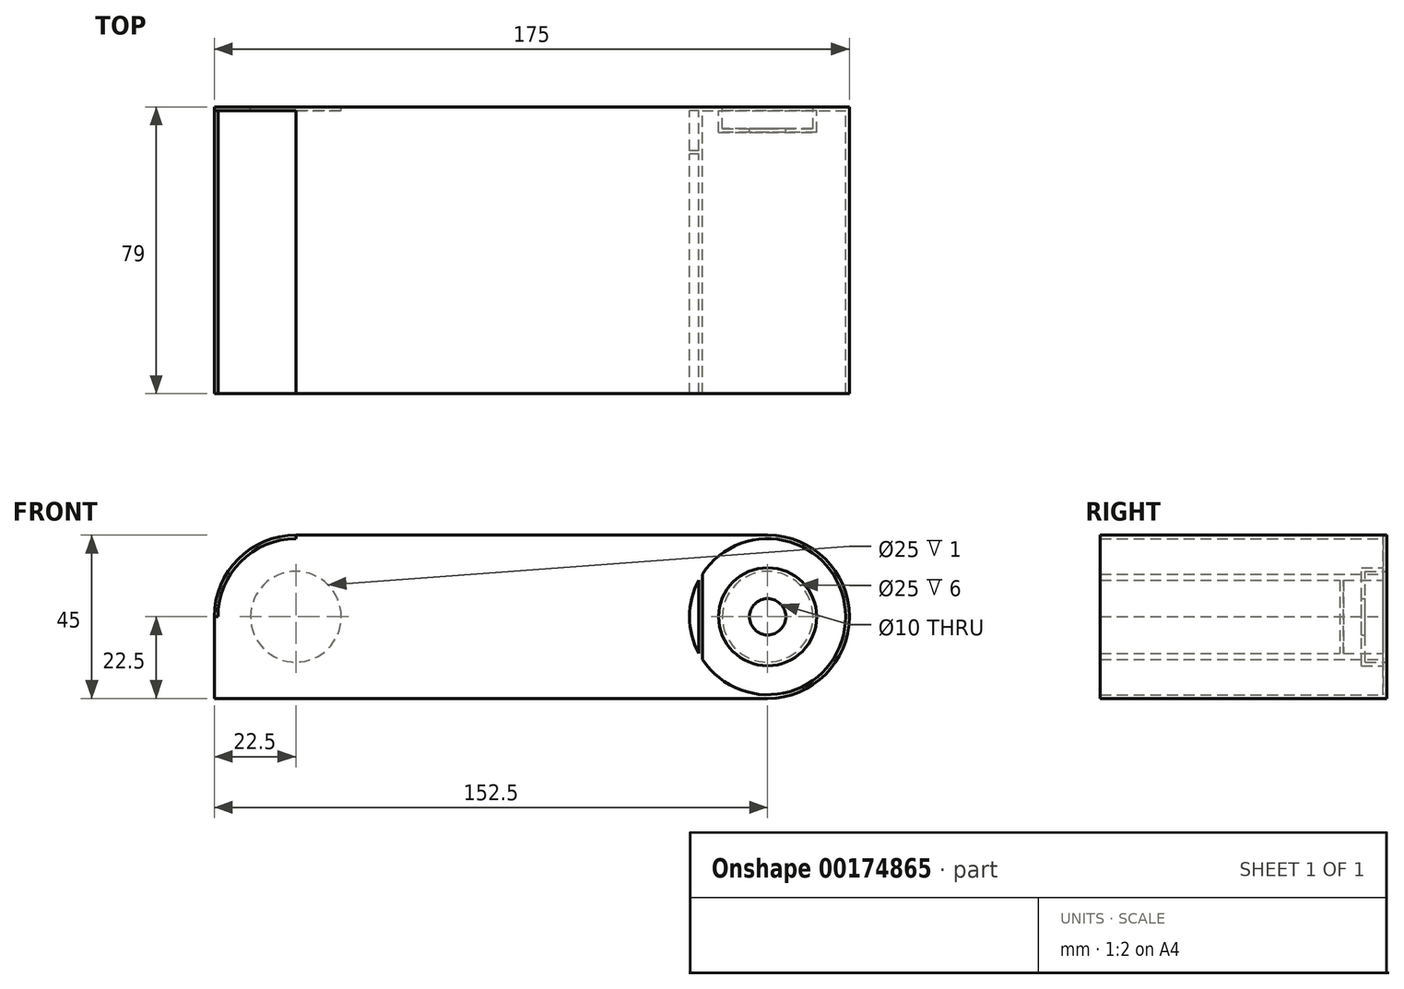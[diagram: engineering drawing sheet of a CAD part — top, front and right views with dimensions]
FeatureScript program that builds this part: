
annotation { "Feature Type Name" : "Feature", "Feature Type Description" : "" }
export const myFeature = defineFeature(function(context is Context, id is Id, definition is map)
    precondition{}
    {
        {
            var Q0;
            Q0=qCreatedBy(makeId("Front.planeOp"),FACE);
            var sketch = newSketch(context, id + "F0", { "sketchPlane" : qUnion([Q0])});
            skLineSegment(sketch, "E0.bottom", {"start": v(82.5, 22.5) * mm, "end": v(-82.5, 22.5) * mm});
            skLineSegment(sketch, "E0.top", {"start": v(82.5, -22.5) * mm, "end": v(-82.5, -22.5) * mm});
            skLineSegment(sketch, "E0.left", {"start": v(82.5, 22.5) * mm, "end": v(82.5, -22.5) * mm});
            skLineSegment(sketch, "E0.right", {"start": v(-82.5, 22.5) * mm, "end": v(-82.5, -22.5) * mm});
            skPoint(sketch, "E0.middle", {"position": v(0, 0) * mm});
            skCircle(sketch, "E1", {"center": v(-65, 0) * mm, "radius": 12.5 * mm});
            skCircle(sketch, "E2", {"center": v(65, 0) * mm, "radius": 12.5 * mm});
            skSolve(sketch);
        }
        {
            var Q0;
            Q0=qSketchRegion(id+"F0",true);
            extrude(context, id + "F1", {"entities" : qUnion([Q0]), "depth" : 1 * mm});
        }
        {
            var Q0;
            Q0=makeQuery(id+"F1.opExtrude","CAP_FACE",FACE,{"disambiguationData":[OSD([sQuery(id+"F0.wireOp",EDGE,"E0.bottom"),sQuery(id+"F0.wireOp",EDGE,"E0.top"),sQuery(id+"F0.wireOp",EDGE,"E0.left"),sQuery(id+"F0.wireOp",EDGE,"E0.right"),sQuery(id+"F0.wireOp",EDGE,"E1"),sQuery(id+"F0.wireOp",EDGE,"E2")])],"isStart":false});
            var sketch = newSketch(context, id + "F2", { "sketchPlane" : qUnion([Q0])});
            skArc(sketch, "E3", {"start": v(65, -22.5) * mm, "mid": v(87.5, 0) * mm, "end": v(65, 22.5) * mm});
            skPoint(sketch, "E4.end.orphan", {"position": v(-82.5, 0) * mm});
            skArc(sketch, "E5", {"start": v(-65, 22.5) * mm, "mid": v(-87.5, 0) * mm, "end": v(-65, -22.5) * mm});
            skLineSegment(sketch, "E6", {"start": v(-65, 22.5) * mm, "end": v(-65, 14.96) * mm});
            skLineSegment(sketch, "E7", {"start": v(-65, 14.96) * mm, "end": v(-75.45, 11.76) * mm});
            skLineSegment(sketch, "E8", {"start": v(-75.45, 11.76) * mm, "end": v(-79.56, 6.47) * mm});
            skLineSegment(sketch, "E9", {"start": v(-79.56, 6.47) * mm, "end": v(-79.56, 0) * mm});
            skLineSegment(sketch, "E10", {"start": v(-79.56, 0) * mm, "end": v(-76.59, -7.8) * mm});
            skLineSegment(sketch, "E11", {"start": v(-76.59, -7.8) * mm, "end": v(-72.84, -12.91) * mm});
            skLineSegment(sketch, "E12", {"start": v(-72.84, -12.91) * mm, "end": v(-67.48, -15.7) * mm});
            skLineSegment(sketch, "E13", {"start": v(-67.48, -15.7) * mm, "end": v(-65, -22.5) * mm});
            skLineSegment(sketch, "E14", {"start": v(65, 22.5) * mm, "end": v(71.47, 16.28) * mm});
            skLineSegment(sketch, "E15", {"start": v(71.47, 16.28) * mm, "end": v(77.4, 9.11) * mm});
            skLineSegment(sketch, "E16", {"start": v(77.4, 9.11) * mm, "end": v(80.4, 2.14) * mm});
            skLineSegment(sketch, "E17", {"start": v(80.4, 2.14) * mm, "end": v(80.4, -5.23) * mm});
            skLineSegment(sketch, "E18", {"start": v(80.4, -5.23) * mm, "end": v(78.4, -12.15) * mm});
            skLineSegment(sketch, "E19", {"start": v(78.4, -12.15) * mm, "end": v(74.66, -14.4) * mm});
            skLineSegment(sketch, "E20", {"start": v(74.66, -14.4) * mm, "end": v(68.4, -19.1) * mm});
            skLineSegment(sketch, "E21", {"start": v(68.4, -19.1) * mm, "end": v(65, -22.5) * mm});
            skSolve(sketch);
        }
        {
            var Q0;
            Q0=qSketchRegion(id+"F2",true);
            extrude(context, id + "F3", {"entities" : qUnion([Q0]), "operationType" : NewBodyOperationType.ADD, "oppositeDirection" : true, "depth" : 1 * mm});
        }
        {
            var Q0;
            {var subQ1=makeQuery(id+"F1.opExtrude","CAP_EDGE",EDGE,{"disambiguationData":[OSD([sQuery(id+"F0.wireOp",EDGE,"E0.bottom")])],"isStart":false});var subQ3=makeQuery(id+"F1.opExtrude","CAP_EDGE",EDGE,{"disambiguationData":[OSD([sQuery(id+"F0.wireOp",EDGE,"E0.right")])],"isStart":false});var subQ5=makeQuery(id+"F2.imprint","INTERSECT",VERTEX,{"derivedFrom":[subQ1,subQ3]});Q0=makeQuery(id+"F2.imprint","IMPRINT",FACE,{"disambiguationData":[TD([[makeQuery(id+"F2.imprint","IMPRINT",EDGE,{"disambiguationData":[TD([[subQ5,-1.0]])],"derivedFrom":subQ3}),1.0]])]});}
            extrude(context, id + "F4", {"entities" : qUnion([Q0]), "operationType" : NewBodyOperationType.REMOVE, "oppositeDirection" : true, "depth" : 25 * mm});
        }
        {
            var Q0;
            {var subQ1=makeQuery(id+"F1.opExtrude","CAP_EDGE",EDGE,{"disambiguationData":[OSD([sQuery(id+"F0.wireOp",EDGE,"E0.top")])],"isStart":false});var subQ3=makeQuery(id+"F1.opExtrude","CAP_EDGE",EDGE,{"disambiguationData":[OSD([sQuery(id+"F0.wireOp",EDGE,"E0.left")])],"isStart":false});var subQ5=makeQuery(id+"F2.imprint","INTERSECT",VERTEX,{"derivedFrom":[subQ1,subQ3]});Q0=makeQuery(id+"F2.imprint","IMPRINT",FACE,{"disambiguationData":[TD([[makeQuery(id+"F2.imprint","IMPRINT",EDGE,{"disambiguationData":[TD([[subQ5,1.0]])],"derivedFrom":subQ3}),-1.0]])]});}
            var Q1;
            {var subQ1=makeQuery(id+"F1.opExtrude","CAP_EDGE",EDGE,{"disambiguationData":[OSD([sQuery(id+"F0.wireOp",EDGE,"E0.bottom")])],"isStart":false});var subQ3=makeQuery(id+"F1.opExtrude","CAP_EDGE",EDGE,{"disambiguationData":[OSD([sQuery(id+"F0.wireOp",EDGE,"E0.left")])],"isStart":false});var subQ5=makeQuery(id+"F2.imprint","INTERSECT",VERTEX,{"derivedFrom":[subQ1,subQ3]});Q1=makeQuery(id+"F2.imprint","IMPRINT",FACE,{"disambiguationData":[TD([[makeQuery(id+"F2.imprint","IMPRINT",EDGE,{"disambiguationData":[TD([[subQ5,-1.0]])],"derivedFrom":subQ3}),-1.0]])]});}
            var Q2;
            {var subQ1=makeQuery(id+"F1.opExtrude","CAP_EDGE",EDGE,{"disambiguationData":[OSD([sQuery(id+"F0.wireOp",EDGE,"E0.top")])],"isStart":false});var subQ3=makeQuery(id+"F1.opExtrude","CAP_EDGE",EDGE,{"disambiguationData":[OSD([sQuery(id+"F0.wireOp",EDGE,"E0.right")])],"isStart":false});var subQ5=makeQuery(id+"F2.imprint","INTERSECT",VERTEX,{"derivedFrom":[subQ1,subQ3]});Q2=makeQuery(id+"F2.imprint","IMPRINT",FACE,{"disambiguationData":[TD([[makeQuery(id+"F2.imprint","IMPRINT",EDGE,{"disambiguationData":[TD([[subQ5,1.0]])],"derivedFrom":subQ3}),1.0]])]});}
            extrude(context, id + "F5", {"entities" : qUnion([Q0, Q1, Q2]), "operationType" : NewBodyOperationType.REMOVE, "oppositeDirection" : true, "depth" : 25 * mm});
        }
        {
            var Q0;
            Q0=makeQuery(id+"F3.boolean.opBoolean","MERGE",FACE,{"derivedFrom":[makeQuery(id+"F1.opExtrude","CAP_FACE",FACE,{"disambiguationData":[OSD([sQuery(id+"F0.wireOp",EDGE,"E0.bottom"),sQuery(id+"F0.wireOp",EDGE,"E0.top"),sQuery(id+"F0.wireOp",EDGE,"E0.left"),sQuery(id+"F0.wireOp",EDGE,"E0.right"),sQuery(id+"F0.wireOp",EDGE,"E1"),sQuery(id+"F0.wireOp",EDGE,"E2")])],"isStart":false}),makeQuery(id+"F3.opExtrude","CAP_FACE",FACE,{"disambiguationData":[OSD([sQuery(id+"F2.wireOp",EDGE,"E3"),sQuery(id+"F2.wireOp",EDGE,"E14"),sQuery(id+"F2.wireOp",EDGE,"E15"),sQuery(id+"F2.wireOp",EDGE,"E16"),sQuery(id+"F2.wireOp",EDGE,"E17"),sQuery(id+"F2.wireOp",EDGE,"E18"),sQuery(id+"F2.wireOp",EDGE,"E19"),sQuery(id+"F2.wireOp",EDGE,"E20"),sQuery(id+"F2.wireOp",EDGE,"E21")])],"isStart":true}),makeQuery(id+"F3.opExtrude","CAP_FACE",FACE,{"disambiguationData":[OSD([sQuery(id+"F2.wireOp",EDGE,"E5"),sQuery(id+"F2.wireOp",EDGE,"E6"),sQuery(id+"F2.wireOp",EDGE,"E7"),sQuery(id+"F2.wireOp",EDGE,"E8"),sQuery(id+"F2.wireOp",EDGE,"E9"),sQuery(id+"F2.wireOp",EDGE,"E10"),sQuery(id+"F2.wireOp",EDGE,"E11"),sQuery(id+"F2.wireOp",EDGE,"E12"),sQuery(id+"F2.wireOp",EDGE,"E13")])],"isStart":true})]});
            var sketch = newSketch(context, id + "F6", { "sketchPlane" : qUnion([Q0])});
            skCircle(sketch, "E22", {"center": v(-65, 0) * mm, "radius": 12.5 * mm});
            skCircle(sketch, "E23", {"center": v(-65, 0) * mm, "radius": 13.5 * mm});
            skCircle(sketch, "E24", {"center": v(65, 0) * mm, "radius": 12.5 * mm});
            skCircle(sketch, "E25", {"center": v(65, 0) * mm, "radius": 13.5 * mm});
            skSolve(sketch);
        }
        {
            var Q0;
            Q0=qSketchRegion(id+"F6",true);
            extrude(context, id + "F7", {"entities" : qUnion([Q0]), "operationType" : NewBodyOperationType.ADD, "depth" : 5 * mm});
        }
        {
            var Q0;
            Q0=makeQuery(id+"F7.opExtrude","CAP_FACE",FACE,{"disambiguationData":[OSD([sQuery(id+"F6.wireOp",EDGE,"E22"),sQuery(id+"F6.wireOp",EDGE,"E23")])],"isStart":false});
            var sketch = newSketch(context, id + "F8", { "sketchPlane" : qUnion([Q0])});
            skCircle(sketch, "E26", {"center": v(-65, 0) * mm, "radius": 13.5 * mm});
            skCircle(sketch, "E27", {"center": v(-65, 0) * mm, "radius": 5 * mm});
            skCircle(sketch, "E28", {"center": v(65, 0) * mm, "radius": 13.5 * mm});
            skCircle(sketch, "E29", {"center": v(65, 0) * mm, "radius": 5 * mm});
            skSolve(sketch);
        }
        {
            var Q0;
            Q0=qSketchRegion(id+"F8",true);
            extrude(context, id + "F9", {"entities" : qUnion([Q0]), "operationType" : NewBodyOperationType.ADD, "depth" : 1 * mm});
        }
        {
            var Q0;
            Q0=makeQuery(id+"F3.boolean.opBoolean","MERGE",FACE,{"derivedFrom":[makeQuery(id+"F1.opExtrude","CAP_FACE",FACE,{"disambiguationData":[OSD([sQuery(id+"F0.wireOp",EDGE,"E0.bottom"),sQuery(id+"F0.wireOp",EDGE,"E0.top"),sQuery(id+"F0.wireOp",EDGE,"E0.left"),sQuery(id+"F0.wireOp",EDGE,"E0.right"),sQuery(id+"F0.wireOp",EDGE,"E1"),sQuery(id+"F0.wireOp",EDGE,"E2")])],"isStart":false}),makeQuery(id+"F3.opExtrude","CAP_FACE",FACE,{"disambiguationData":[OSD([sQuery(id+"F2.wireOp",EDGE,"E3"),sQuery(id+"F2.wireOp",EDGE,"E14"),sQuery(id+"F2.wireOp",EDGE,"E15"),sQuery(id+"F2.wireOp",EDGE,"E16"),sQuery(id+"F2.wireOp",EDGE,"E17"),sQuery(id+"F2.wireOp",EDGE,"E18"),sQuery(id+"F2.wireOp",EDGE,"E19"),sQuery(id+"F2.wireOp",EDGE,"E20"),sQuery(id+"F2.wireOp",EDGE,"E21")])],"isStart":true}),makeQuery(id+"F3.opExtrude","CAP_FACE",FACE,{"disambiguationData":[OSD([sQuery(id+"F2.wireOp",EDGE,"E5"),sQuery(id+"F2.wireOp",EDGE,"E6"),sQuery(id+"F2.wireOp",EDGE,"E7"),sQuery(id+"F2.wireOp",EDGE,"E8"),sQuery(id+"F2.wireOp",EDGE,"E9"),sQuery(id+"F2.wireOp",EDGE,"E10"),sQuery(id+"F2.wireOp",EDGE,"E11"),sQuery(id+"F2.wireOp",EDGE,"E12"),sQuery(id+"F2.wireOp",EDGE,"E13")])],"isStart":true})]});
            var sketch = newSketch(context, id + "F10", { "sketchPlane" : qUnion([Q0])});
            skLineSegment(sketch, "E30.bottom", {"start": v(-87.5, 0) * mm, "end": v(-81.94, 0) * mm});
            skLineSegment(sketch, "E30.top", {"start": v(-87.5, -22.5) * mm, "end": v(-65, -22.5) * mm});
            skLineSegment(sketch, "E30.left", {"start": v(-87.5, 0) * mm, "end": v(-87.5, -22.5) * mm});
            skLineSegment(sketch, "E30.right", {"start": v(-65, -18.59) * mm, "end": v(-65, -22.5) * mm});
            skLineSegment(sketch, "E31", {"start": v(-81.94, 0) * mm, "end": v(-80.2, -9.62) * mm});
            skLineSegment(sketch, "E32", {"start": v(-80.2, -9.62) * mm, "end": v(-73.32, -16) * mm});
            skLineSegment(sketch, "E33", {"start": v(-73.32, -16) * mm, "end": v(-65, -18.59) * mm});
            skSolve(sketch);
        }
        {
            var Q0;
            Q0=qSketchRegion(id+"F10",true);
            extrude(context, id + "F11", {"entities" : qUnion([Q0]), "operationType" : NewBodyOperationType.ADD, "oppositeDirection" : true, "depth" : 1 * mm});
        }
        {
            var Q0;
            Q0=makeQuery(id+"F11.boolean.opBoolean","MERGE",FACE,{"derivedFrom":[makeQuery(id+"F3.boolean.opBoolean","MERGE",FACE,{"derivedFrom":[makeQuery(id+"F1.opExtrude","CAP_FACE",FACE,{"disambiguationData":[OSD([sQuery(id+"F0.wireOp",EDGE,"E0.bottom"),sQuery(id+"F0.wireOp",EDGE,"E0.top"),sQuery(id+"F0.wireOp",EDGE,"E0.left"),sQuery(id+"F0.wireOp",EDGE,"E0.right"),sQuery(id+"F0.wireOp",EDGE,"E1"),sQuery(id+"F0.wireOp",EDGE,"E2")])],"isStart":false}),makeQuery(id+"F3.opExtrude","CAP_FACE",FACE,{"disambiguationData":[OSD([sQuery(id+"F2.wireOp",EDGE,"E3"),sQuery(id+"F2.wireOp",EDGE,"E14"),sQuery(id+"F2.wireOp",EDGE,"E15"),sQuery(id+"F2.wireOp",EDGE,"E16"),sQuery(id+"F2.wireOp",EDGE,"E17"),sQuery(id+"F2.wireOp",EDGE,"E18"),sQuery(id+"F2.wireOp",EDGE,"E19"),sQuery(id+"F2.wireOp",EDGE,"E20"),sQuery(id+"F2.wireOp",EDGE,"E21")])],"isStart":true}),makeQuery(id+"F3.opExtrude","CAP_FACE",FACE,{"disambiguationData":[OSD([sQuery(id+"F2.wireOp",EDGE,"E5"),sQuery(id+"F2.wireOp",EDGE,"E6"),sQuery(id+"F2.wireOp",EDGE,"E7"),sQuery(id+"F2.wireOp",EDGE,"E8"),sQuery(id+"F2.wireOp",EDGE,"E9"),sQuery(id+"F2.wireOp",EDGE,"E10"),sQuery(id+"F2.wireOp",EDGE,"E11"),sQuery(id+"F2.wireOp",EDGE,"E12"),sQuery(id+"F2.wireOp",EDGE,"E13")])],"isStart":true})]}),makeQuery(id+"F11.opExtrude","CAP_FACE",FACE,{"disambiguationData":[OSD([sQuery(id+"F10.wireOp",EDGE,"E30.bottom"),sQuery(id+"F10.wireOp",EDGE,"E30.top"),sQuery(id+"F10.wireOp",EDGE,"E30.left"),sQuery(id+"F10.wireOp",EDGE,"E30.right"),sQuery(id+"F10.wireOp",EDGE,"E31"),sQuery(id+"F10.wireOp",EDGE,"E32"),sQuery(id+"F10.wireOp",EDGE,"E33")])],"isStart":true})]});
            var sketch = newSketch(context, id + "F12", { "sketchPlane" : qUnion([Q0])});
            skLineSegment(sketch, "E34.bottom", {"start": v(47, -13.5) * mm, "end": v(-47, -13.5) * mm});
            skLineSegment(sketch, "E34.top", {"start": v(47, -14.5) * mm, "end": v(-47, -14.5) * mm});
            skLineSegment(sketch, "E34.left", {"start": v(47, -13.5) * mm, "end": v(47, -14.5) * mm});
            skLineSegment(sketch, "E34.right", {"start": v(-47, -13.5) * mm, "end": v(-47, -14.5) * mm});
            skPoint(sketch, "E34.middle", {"position": v(0, -14) * mm});
            skLineSegment(sketch, "E35.bottom", {"start": v(-47, -14.5) * mm, "end": v(-46, -14.5) * mm});
            skLineSegment(sketch, "E35.top", {"start": v(-47, 22.5) * mm, "end": v(-46, 22.5) * mm});
            skLineSegment(sketch, "E35.left", {"start": v(-47, -14.5) * mm, "end": v(-47, 22.5) * mm});
            skLineSegment(sketch, "E35.right", {"start": v(-46, -14.5) * mm, "end": v(-46, 22.5) * mm});
            skLineSegment(sketch, "E36.bottom", {"start": v(47, -14.5) * mm, "end": v(46, -14.5) * mm});
            skLineSegment(sketch, "E36.top", {"start": v(47, 22.5) * mm, "end": v(46, 22.5) * mm});
            skLineSegment(sketch, "E36.left", {"start": v(47, -14.5) * mm, "end": v(47, 22.5) * mm});
            skLineSegment(sketch, "E36.right", {"start": v(46, -14.5) * mm, "end": v(46, 22.5) * mm});
            skSolve(sketch);
        }
        {
            var Q0;
            Q0=qSketchRegion(id+"F12",true);
            extrude(context, id + "F13", {"entities" : qUnion([Q0]), "operationType" : NewBodyOperationType.ADD, "depth" : 11 * mm});
        }
        {
            var Q0;
            Q0=makeQuery(id+"F13.opExtrude","CAP_FACE",FACE,{"disambiguationData":[OSD([sQuery(id+"F12.wireOp",EDGE,"E34.bottom"),sQuery(id+"F12.wireOp",EDGE,"E34.top"),sQuery(id+"F12.wireOp",EDGE,"E35.bottom"),sQuery(id+"F12.wireOp",EDGE,"E35.top"),sQuery(id+"F12.wireOp",EDGE,"E35.left"),sQuery(id+"F12.wireOp",EDGE,"E35.right"),sQuery(id+"F12.wireOp",EDGE,"E36.bottom"),sQuery(id+"F12.wireOp",EDGE,"E36.top"),sQuery(id+"F12.wireOp",EDGE,"E36.left"),sQuery(id+"F12.wireOp",EDGE,"E36.right")])],"isStart":false});
            var sketch = newSketch(context, id + "F14", { "sketchPlane" : qUnion([Q0])});
            skLineSegment(sketch, "E37.bottom", {"start": v(-47, -14.5) * mm, "end": v(47, -14.5) * mm});
            skLineSegment(sketch, "E37.top", {"start": v(-47, 22.5) * mm, "end": v(47, 22.5) * mm});
            skLineSegment(sketch, "E37.left", {"start": v(-47, -14.5) * mm, "end": v(-47, 22.5) * mm});
            skLineSegment(sketch, "E37.right", {"start": v(47, -14.5) * mm, "end": v(47, 22.5) * mm});
            skSolve(sketch);
        }
        {
            var Q0;
            Q0=qSketchRegion(id+"F14",true);
            extrude(context, id + "F15", {"entities" : qUnion([Q0]), "operationType" : NewBodyOperationType.ADD, "depth" : 1 * mm});
        }
        {
            var Q0;
            Q0=makeQuery(id+"F15.opExtrude","CAP_FACE",FACE,{"disambiguationData":[OSD([sQuery(id+"F14.wireOp",EDGE,"E37.bottom"),sQuery(id+"F14.wireOp",EDGE,"E37.top"),sQuery(id+"F14.wireOp",EDGE,"E37.left"),sQuery(id+"F14.wireOp",EDGE,"E37.right")])],"isStart":false});
            var sketch = newSketch(context, id + "F16", { "sketchPlane" : qUnion([Q0])});
            skLineSegment(sketch, "E38.bottom", {"start": v(-47, 22.5) * mm, "end": v(-46, 22.5) * mm});
            skLineSegment(sketch, "E38.top", {"start": v(-47, -13.5) * mm, "end": v(-46, -13.5) * mm});
            skLineSegment(sketch, "E38.left", {"start": v(-47, 22.5) * mm, "end": v(-47, -13.5) * mm});
            skLineSegment(sketch, "E38.right", {"start": v(-46, 22.5) * mm, "end": v(-46, -13.5) * mm});
            skLineSegment(sketch, "E39.bottom", {"start": v(47, 22.5) * mm, "end": v(46, 22.5) * mm});
            skLineSegment(sketch, "E39.top", {"start": v(47, -13.5) * mm, "end": v(46, -13.5) * mm});
            skLineSegment(sketch, "E39.left", {"start": v(47, 22.5) * mm, "end": v(47, -13.5) * mm});
            skLineSegment(sketch, "E39.right", {"start": v(46, 22.5) * mm, "end": v(46, -13.5) * mm});
            skSolve(sketch);
        }
        {
            var Q0;
            Q0=qSketchRegion(id+"F16",true);
            extrude(context, id + "F17", {"entities" : qUnion([Q0]), "operationType" : NewBodyOperationType.ADD, "depth" : 66 * mm});
        }
        {
            var Q0;
            {var subQ0=sQuery(id+"F2.wireOp",EDGE,"E14");var subQ1=sQuery(id+"F2.wireOp",EDGE,"E3");var subQ2=sQuery(id+"F0.wireOp",EDGE,"E0.bottom");var subQ3=sQuery(id+"F0.wireOp",EDGE,"E0.left");var subQ5=sQuery(id+"F2.wireOp",EDGE,"E21");var subQ6=sQuery(id+"F0.wireOp",EDGE,"E0.top");var subQ7=sQuery(id+"F2.wireOp",EDGE,"E5");var subQ8=sQuery(id+"F10.wireOp",EDGE,"E30.top");var subQ9=sQuery(id+"F10.wireOp",EDGE,"E30.left");Q0=makeQuery(id+"F13.boolean.opBoolean","SPLIT",FACE,{"disambiguationData":[TD([makeQuery(id+"F1.opExtrude","SWEPT_FACE",FACE,{"disambiguationData":[OSD([subQ6])]})])],"derivedFrom":makeQuery(id+"F11.boolean.opBoolean","MERGE",FACE,{"derivedFrom":[makeQuery(id+"F3.boolean.opBoolean","MERGE",FACE,{"derivedFrom":[makeQuery(id+"F1.opExtrude","CAP_FACE",FACE,{"disambiguationData":[OSD([subQ2,subQ6,subQ3,sQuery(id+"F0.wireOp",EDGE,"E0.right"),sQuery(id+"F0.wireOp",EDGE,"E1"),sQuery(id+"F0.wireOp",EDGE,"E2")])],"isStart":false}),makeQuery(id+"F3.opExtrude","CAP_FACE",FACE,{"disambiguationData":[OSD([subQ1,subQ0,sQuery(id+"F2.wireOp",EDGE,"E15"),sQuery(id+"F2.wireOp",EDGE,"E16"),sQuery(id+"F2.wireOp",EDGE,"E17"),sQuery(id+"F2.wireOp",EDGE,"E18"),sQuery(id+"F2.wireOp",EDGE,"E19"),sQuery(id+"F2.wireOp",EDGE,"E20"),subQ5])],"isStart":true}),makeQuery(id+"F3.opExtrude","CAP_FACE",FACE,{"disambiguationData":[OSD([subQ7,sQuery(id+"F2.wireOp",EDGE,"E6"),sQuery(id+"F2.wireOp",EDGE,"E7"),sQuery(id+"F2.wireOp",EDGE,"E8"),sQuery(id+"F2.wireOp",EDGE,"E9"),sQuery(id+"F2.wireOp",EDGE,"E10"),sQuery(id+"F2.wireOp",EDGE,"E11"),sQuery(id+"F2.wireOp",EDGE,"E12"),sQuery(id+"F2.wireOp",EDGE,"E13")])],"isStart":true})]}),makeQuery(id+"F11.opExtrude","CAP_FACE",FACE,{"disambiguationData":[OSD([sQuery(id+"F10.wireOp",EDGE,"E30.bottom"),subQ8,subQ9,sQuery(id+"F10.wireOp",EDGE,"E30.right"),sQuery(id+"F10.wireOp",EDGE,"E31"),sQuery(id+"F10.wireOp",EDGE,"E32"),sQuery(id+"F10.wireOp",EDGE,"E33")])],"isStart":true})]})});}
            var sketch = newSketch(context, id + "F18", { "sketchPlane" : qUnion([Q0])});
            skLineSegment(sketch, "E40.bottom", {"start": v(-13.08, -10.5) * mm, "end": v(13.2, -10.5) * mm});
            skLineSegment(sketch, "E40.top", {"start": v(-13.08, -11.5) * mm, "end": v(13.2, -11.5) * mm});
            skLineSegment(sketch, "E40.left", {"start": v(-13.08, -10.5) * mm, "end": v(-13.08, -11.5) * mm});
            skLineSegment(sketch, "E40.right", {"start": v(13.2, -10.5) * mm, "end": v(13.2, -11.5) * mm});
            skSolve(sketch);
        }
        {
            var Q0;
            Q0=qSketchRegion(id+"F18",true);
            extrude(context, id + "F19", {"entities" : qUnion([Q0]), "operationType" : NewBodyOperationType.ADD, "depth" : 3 * mm});
        }
        {
            var Q0;
            {var subQ0=sQuery(id+"F2.wireOp",EDGE,"E14");var subQ1=sQuery(id+"F2.wireOp",EDGE,"E3");var subQ2=sQuery(id+"F0.wireOp",EDGE,"E0.bottom");var subQ3=sQuery(id+"F0.wireOp",EDGE,"E0.left");var subQ5=sQuery(id+"F2.wireOp",EDGE,"E21");var subQ6=sQuery(id+"F0.wireOp",EDGE,"E0.top");var subQ7=sQuery(id+"F2.wireOp",EDGE,"E5");var subQ8=sQuery(id+"F10.wireOp",EDGE,"E30.top");var subQ9=sQuery(id+"F10.wireOp",EDGE,"E30.left");Q0=makeQuery(id+"F13.boolean.opBoolean","SPLIT",FACE,{"disambiguationData":[TD([makeQuery(id+"F1.opExtrude","SWEPT_FACE",FACE,{"disambiguationData":[OSD([subQ6])]})])],"derivedFrom":makeQuery(id+"F11.boolean.opBoolean","MERGE",FACE,{"derivedFrom":[makeQuery(id+"F3.boolean.opBoolean","MERGE",FACE,{"derivedFrom":[makeQuery(id+"F1.opExtrude","CAP_FACE",FACE,{"disambiguationData":[OSD([subQ2,subQ6,subQ3,sQuery(id+"F0.wireOp",EDGE,"E0.right"),sQuery(id+"F0.wireOp",EDGE,"E1"),sQuery(id+"F0.wireOp",EDGE,"E2")])],"isStart":false}),makeQuery(id+"F3.opExtrude","CAP_FACE",FACE,{"disambiguationData":[OSD([subQ1,subQ0,sQuery(id+"F2.wireOp",EDGE,"E15"),sQuery(id+"F2.wireOp",EDGE,"E16"),sQuery(id+"F2.wireOp",EDGE,"E17"),sQuery(id+"F2.wireOp",EDGE,"E18"),sQuery(id+"F2.wireOp",EDGE,"E19"),sQuery(id+"F2.wireOp",EDGE,"E20"),subQ5])],"isStart":true}),makeQuery(id+"F3.opExtrude","CAP_FACE",FACE,{"disambiguationData":[OSD([subQ7,sQuery(id+"F2.wireOp",EDGE,"E6"),sQuery(id+"F2.wireOp",EDGE,"E7"),sQuery(id+"F2.wireOp",EDGE,"E8"),sQuery(id+"F2.wireOp",EDGE,"E9"),sQuery(id+"F2.wireOp",EDGE,"E10"),sQuery(id+"F2.wireOp",EDGE,"E11"),sQuery(id+"F2.wireOp",EDGE,"E12"),sQuery(id+"F2.wireOp",EDGE,"E13")])],"isStart":true})]}),makeQuery(id+"F11.opExtrude","CAP_FACE",FACE,{"disambiguationData":[OSD([sQuery(id+"F10.wireOp",EDGE,"E30.bottom"),subQ8,subQ9,sQuery(id+"F10.wireOp",EDGE,"E30.right"),sQuery(id+"F10.wireOp",EDGE,"E31"),sQuery(id+"F10.wireOp",EDGE,"E32"),sQuery(id+"F10.wireOp",EDGE,"E33")])],"isStart":true})]})});}
            var sketch = newSketch(context, id + "F20", { "sketchPlane" : qUnion([Q0])});
            skLineSegment(sketch, "E41", {"start": v(-65, 22.5) * mm, "end": v(65, 22.5) * mm});
            skLineSegment(sketch, "E42", {"start": v(65, 22.5) * mm, "end": v(65, -22.5) * mm});
            skLineSegment(sketch, "E43", {"start": v(65, -22.5) * mm, "end": v(-87.5, -22.5) * mm});
            skLineSegment(sketch, "E44", {"start": v(-87.5, -22.5) * mm, "end": v(-87.5, 0) * mm});
            skArc(sketch, "E45", {"start": v(65, -22.5) * mm, "mid": v(87.5, 0) * mm, "end": v(65, 22.5) * mm});
            skLineSegment(sketch, "E46", {"start": v(65, 21.5) * mm, "end": v(-65, 21.5) * mm});
            skLineSegment(sketch, "E47", {"start": v(-65, 21.5) * mm, "end": v(-65, 22.5) * mm});
            skLineSegment(sketch, "E48", {"start": v(-87.5, 0) * mm, "end": v(-86.5, 0) * mm});
            skLineSegment(sketch, "E49", {"start": v(-86.5, 0) * mm, "end": v(-86.5, -22.5) * mm});
            skLineSegment(sketch, "E50", {"start": v(-86.5, -22.5) * mm, "end": v(-86.5, -21.5) * mm});
            skLineSegment(sketch, "E51", {"start": v(-86.5, -21.5) * mm, "end": v(65, -21.5) * mm});
            skLineSegment(sketch, "E52", {"start": v(65, -21.5) * mm, "end": v(62.41, -21.5) * mm});
            skArc(sketch, "E53", {"start": v(-65, 21.5) * mm, "mid": v(-80.2, 15.2) * mm, "end": v(-86.5, 0) * mm});
            skCircle(sketch, "E54", {"center": v(65, 0) * mm, "radius": 21.5 * mm});
            skSolve(sketch);
        }
        {
            var Q0;
            Q0 = qSketchRegion(id + "F20", true);
            extrude(context, id + "F21", {"entities" : qUnion([Q0]), "operationType" : NewBodyOperationType.ADD, "depth" : 78 * mm});
        }
    });
